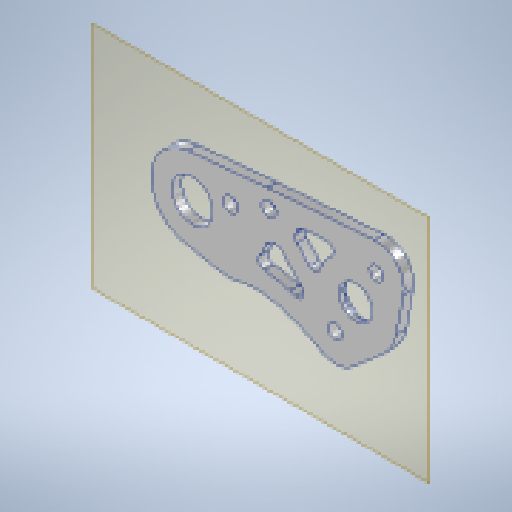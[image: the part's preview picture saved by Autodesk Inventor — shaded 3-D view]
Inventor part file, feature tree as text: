
AUTODESK INVENTOR PART (.ipt)
format: ipt  version: 2023 (Build 270158000, 158)  size: 296,448 bytes
history: native  units: in
note: dims shown in document units (in); Inventor stores cm internally (conversion verified against a paired STEP export)
features: extrude x3, other x3, fillet x2, plane x1, reference x1, sketch x1, projected_geometry x1
ambient origin geometry x8: Origin, YZ Plane, XZ Plane, XY Plane, X Axis, Y Axis, Z Axis, Center Point
bodies: Solid1 (feature_tree)
feature tree (12):
  plane  "Work Plane1"
  extrude  "Extrusion1"  Depth=0.5in
  extrude  "Extrusion2"  Depth=0.054in TaperAngle=0.0deg
  extrude  "Extrusion3"  Depth=1.0in
  fillet  "Fillet1"  Radius=0.18in
  fillet  "Fillet2"  Radius=0.18in
  reference  "Reference1"
  sketch  "Sketch3"  dims[d0=0.1181in d1=0.0in d2=0.05in d3=0.054in d4=0.0in d5=1.0in d6=0.18in d7=0.18in d8=0.5in d9=0.125in d10=0.45in d13=0.25in d14=0.25in d18=0.25in d19=0.1181in d20=0.0in d21=0.0787in d23=1.0in d24=0.5in]
  projected_geometry  "Projected Loop1"
  other  "<userpath> Hah\Documents\GitHub\spin-up-cad\spin-up-18_1\MainAssy.iam"
  other  "MainAssy.iam"
  other  "IntakeForearm:1"
